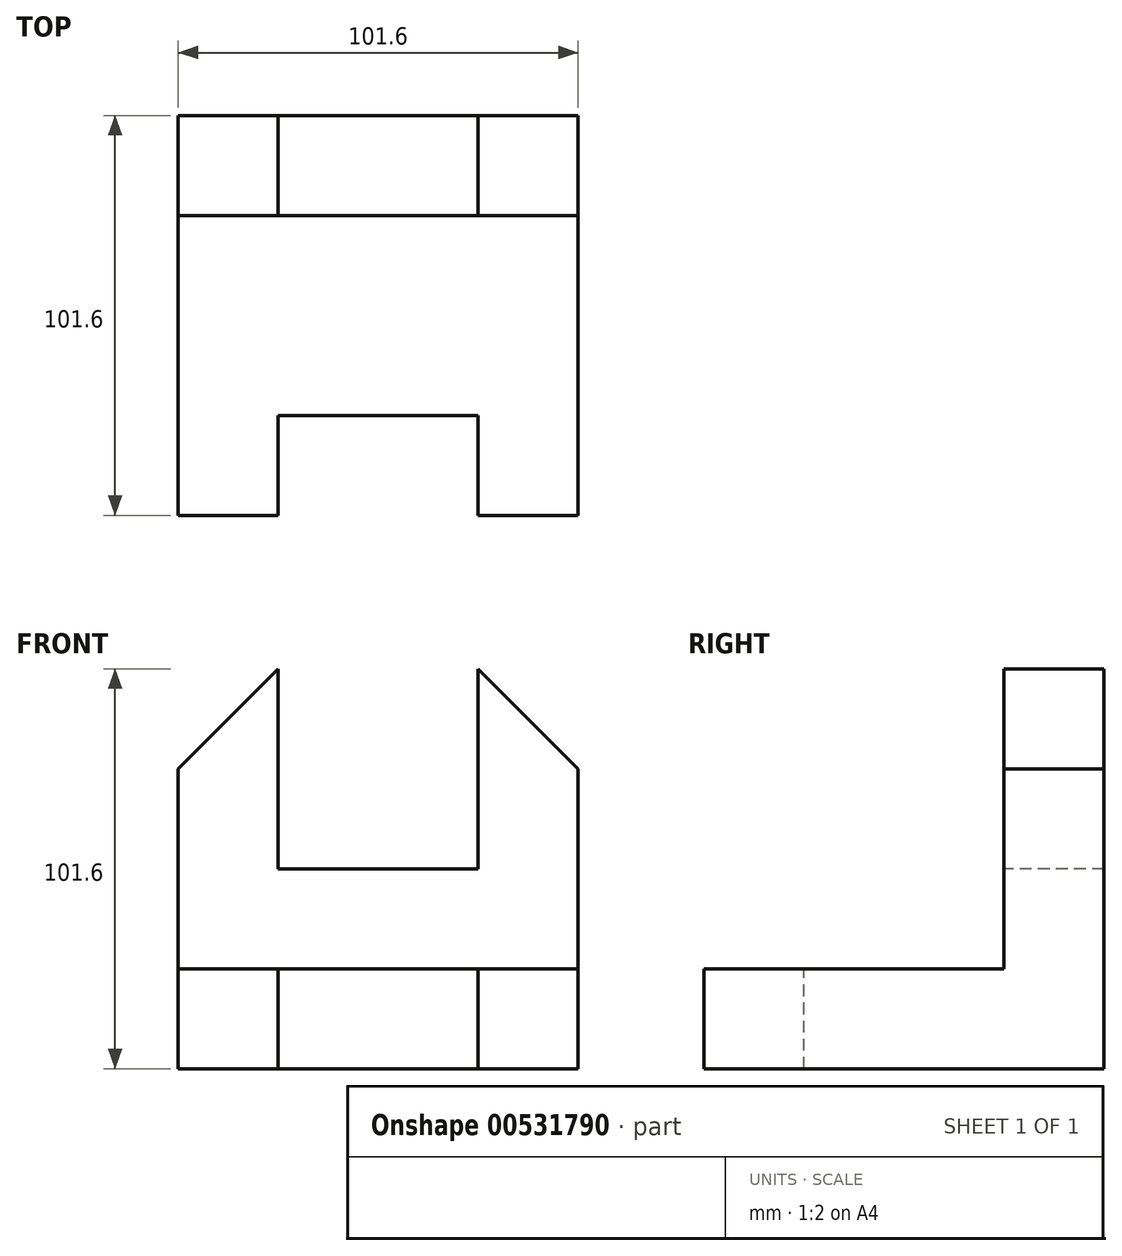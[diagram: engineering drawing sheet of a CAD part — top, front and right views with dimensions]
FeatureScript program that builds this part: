
annotation { "Feature Type Name" : "Feature", "Feature Type Description" : "" }
export const myFeature = defineFeature(function(context is Context, id is Id, definition is map)
    precondition{}
    {
        {
            var Q0;
            Q0=qCreatedBy(makeId("Front.planeOp"),FACE);
            var sketch = newSketch(context, id + "F0", { "sketchPlane" : qUnion([Q0])});
            skLineSegment(sketch, "E0.bottom", {"start": v(-153.66, -86.24) * mm, "end": v(-52.06, -86.24) * mm});
            skLineSegment(sketch, "E0.top", {"start": v(-153.66, 15.36) * mm, "end": v(-52.06, 15.36) * mm});
            skLineSegment(sketch, "E0.left", {"start": v(-153.66, -86.24) * mm, "end": v(-153.66, 15.36) * mm});
            skLineSegment(sketch, "E0.right", {"start": v(-52.06, -86.24) * mm, "end": v(-52.06, 15.36) * mm});
            skSolve(sketch);
        }
        {
            var Q0;
            Q0=makeQuery(id+"F0.imprint","IMPRINT",FACE,{"disambiguationData":[TD([[makeQuery(id+"F0.imprint","IMPRINT",EDGE,{"derivedFrom":sQuery(id+"F0.wireOp",EDGE,"E0.bottom")}),1.0]])]});
            extrude(context, id + "F1", {"entities" : qUnion([Q0]), "depth" : 101.6 * mm, "offsetDistance" : 25.4 * mm});
        }
        {
            var Q0;
            Q0=makeQuery(id+"F1.opExtrude","CAP_FACE",FACE,{"disambiguationData":[OSD([sQuery(id+"F0.wireOp",EDGE,"E0.bottom"),sQuery(id+"F0.wireOp",EDGE,"E0.top"),sQuery(id+"F0.wireOp",EDGE,"E0.left"),sQuery(id+"F0.wireOp",EDGE,"E0.right")])],"isStart":false});
            var sketch = newSketch(context, id + "F2", { "sketchPlane" : qUnion([Q0])});
            skLineSegment(sketch, "E1", {"start": v(-153.66, -86.24) * mm, "end": v(-153.66, -60.84) * mm});
            skLineSegment(sketch, "E2", {"start": v(-153.66, -60.84) * mm, "end": v(-52.06, -60.84) * mm});
            skLineSegment(sketch, "E3.top", {"start": v(-153.66, -10.04) * mm, "end": v(-52.06, -10.04) * mm});
            skLineSegment(sketch, "E3.left", {"start": v(-153.66, -60.84) * mm, "end": v(-153.66, -10.04) * mm});
            skLineSegment(sketch, "E3.right", {"start": v(-52.06, -60.84) * mm, "end": v(-52.06, -10.04) * mm});
            skSolve(sketch);
        }
        {
            var Q0;
            Q0=makeQuery(id+"F2.imprint","IMPRINT",FACE,{"disambiguationData":[TD([[makeQuery(id+"F2.imprint","IMPRINT",EDGE,{"derivedFrom":sQuery(id+"F2.wireOp",EDGE,"E2")}),1.0]])]});
            extrude(context, id + "F3", {"entities" : qUnion([Q0]), "operationType" : NewBodyOperationType.REMOVE, "oppositeDirection" : true, "depth" : 76.2 * mm, "offsetDistance" : 25.4 * mm});
        }
        {
            var Q0;
            {var subQ0=sQuery(id+"F0.wireOp",EDGE,"E0.top");var subQ1=sQuery(id+"F0.wireOp",EDGE,"E0.left");var subQ2=sQuery(id+"F0.wireOp",EDGE,"E0.right");Q0=makeQuery(id+"F3.boolean.opBoolean","SPLIT",FACE,{"disambiguationData":[TD([makeQuery(id+"F1.opExtrude","SWEPT_FACE",FACE,{"disambiguationData":[OSD([subQ0])]})])],"derivedFrom":makeQuery(id+"F1.opExtrude","CAP_FACE",FACE,{"disambiguationData":[OSD([sQuery(id+"F0.wireOp",EDGE,"E0.bottom"),subQ0,subQ1,subQ2])],"isStart":false})});}
            extrude(context, id + "F4", {"entities" : qUnion([Q0]), "operationType" : NewBodyOperationType.REMOVE, "oppositeDirection" : true, "depth" : 76.2 * mm, "offsetDistance" : 25.4 * mm});
        }
        {
            var Q0;
            Q0=makeQuery(id+"F4.boolean.opBoolean","MERGE",FACE,{"derivedFrom":[makeQuery(id+"F3.boolean.opBoolean","COPY",FACE,{"derivedFrom":makeQuery(id+"F3.opExtrude","CAP_FACE",FACE,{"disambiguationData":[OSD([sQuery(id+"F2.wireOp",EDGE,"E2"),sQuery(id+"F2.wireOp",EDGE,"E3.top"),sQuery(id+"F2.wireOp",EDGE,"E3.left"),sQuery(id+"F2.wireOp",EDGE,"E3.right")])],"isStart":false})}),makeQuery(id+"F4.opExtrude","CAP_FACE",FACE,{"disambiguationData":[OSD([sQuery(id+"F0.wireOp",EDGE,"E0.bottom"),sQuery(id+"F0.wireOp",EDGE,"E0.top"),sQuery(id+"F0.wireOp",EDGE,"E0.left"),sQuery(id+"F0.wireOp",EDGE,"E0.right")])],"isStart":false})]});
            var sketch = newSketch(context, id + "F5", { "sketchPlane" : qUnion([Q0])});
            skLineSegment(sketch, "E4.bottom", {"start": v(-153.66, 15.36) * mm, "end": v(-128.26, 15.36) * mm});
            skLineSegment(sketch, "E4.top", {"start": v(-153.66, -35.44) * mm, "end": v(-128.26, -35.44) * mm});
            skLineSegment(sketch, "E4.left", {"start": v(-153.66, 15.36) * mm, "end": v(-153.66, -35.44) * mm});
            skLineSegment(sketch, "E4.right", {"start": v(-128.26, 15.36) * mm, "end": v(-128.26, -35.44) * mm});
            skLineSegment(sketch, "E5.bottom", {"start": v(-52.06, 15.36) * mm, "end": v(-77.46, 15.36) * mm});
            skLineSegment(sketch, "E5.top", {"start": v(-52.06, -35.44) * mm, "end": v(-77.46, -35.44) * mm});
            skLineSegment(sketch, "E5.left", {"start": v(-52.06, 15.36) * mm, "end": v(-52.06, -35.44) * mm});
            skLineSegment(sketch, "E5.right", {"start": v(-77.46, 15.36) * mm, "end": v(-77.46, -35.44) * mm});
            skLineSegment(sketch, "E6", {"start": v(-128.26, -35.44) * mm, "end": v(-77.46, -35.44) * mm});
            skLineSegment(sketch, "E7", {"start": v(-128.26, 15.36) * mm, "end": v(-77.46, 15.36) * mm});
            skSolve(sketch);
        }
        {
            var Q0;
            Q0=makeQuery(id+"F5.imprint","IMPRINT",FACE,{"disambiguationData":[TD([[makeQuery(id+"F5.imprint","IMPRINT",EDGE,{"derivedFrom":sQuery(id+"F5.wireOp",EDGE,"E4.right")}),1.0]])]});
            extrude(context, id + "F6", {"entities" : qUnion([Q0]), "operationType" : NewBodyOperationType.REMOVE, "oppositeDirection" : true, "depth" : 25.4 * mm, "offsetDistance" : 25.4 * mm});
        }
        {
            var Q0;
            Q0=makeQuery(id+"F4.boolean.opBoolean","MERGE",FACE,{"derivedFrom":[makeQuery(id+"F3.boolean.opBoolean","COPY",FACE,{"derivedFrom":makeQuery(id+"F3.opExtrude","CAP_FACE",FACE,{"disambiguationData":[OSD([sQuery(id+"F2.wireOp",EDGE,"E2"),sQuery(id+"F2.wireOp",EDGE,"E3.top"),sQuery(id+"F2.wireOp",EDGE,"E3.left"),sQuery(id+"F2.wireOp",EDGE,"E3.right")])],"isStart":false})}),makeQuery(id+"F4.opExtrude","CAP_FACE",FACE,{"disambiguationData":[OSD([sQuery(id+"F0.wireOp",EDGE,"E0.bottom"),sQuery(id+"F0.wireOp",EDGE,"E0.top"),sQuery(id+"F0.wireOp",EDGE,"E0.left"),sQuery(id+"F0.wireOp",EDGE,"E0.right")])],"isStart":false})]});
            var sketch = newSketch(context, id + "F7", { "sketchPlane" : qUnion([Q0])});
            skLineSegment(sketch, "E8", {"start": v(-153.66, 15.36) * mm, "end": v(-153.66, -10.04) * mm});
            skLineSegment(sketch, "E9", {"start": v(-153.66, -10.04) * mm, "end": v(-128.26, 15.36) * mm});
            skLineSegment(sketch, "E10", {"start": v(-153.66, 15.36) * mm, "end": v(-128.26, 15.36) * mm});
            skLineSegment(sketch, "E11", {"start": v(-52.06, 15.36) * mm, "end": v(-52.06, -10.04) * mm});
            skLineSegment(sketch, "E12", {"start": v(-77.46, 15.36) * mm, "end": v(-52.06, -10.04) * mm});
            skLineSegment(sketch, "E13", {"start": v(-77.46, 15.36) * mm, "end": v(-52.06, 15.36) * mm});
            skSolve(sketch);
        }
        {
            var Q0;
            Q0=makeQuery(id+"F7.imprint","IMPRINT",FACE,{"disambiguationData":[TD([[makeQuery(id+"F7.imprint","IMPRINT",EDGE,{"derivedFrom":sQuery(id+"F7.wireOp",EDGE,"E8")}),-1.0]])]});
            extrude(context, id + "F8", {"entities" : qUnion([Q0]), "operationType" : NewBodyOperationType.REMOVE, "oppositeDirection" : true, "depth" : 25.4 * mm, "offsetDistance" : 25.4 * mm});
        }
        {
            var Q0;
            Q0=makeQuery(id+"F4.boolean.opBoolean","MERGE",FACE,{"derivedFrom":[makeQuery(id+"F3.boolean.opBoolean","COPY",FACE,{"derivedFrom":makeQuery(id+"F3.opExtrude","CAP_FACE",FACE,{"disambiguationData":[OSD([sQuery(id+"F2.wireOp",EDGE,"E2"),sQuery(id+"F2.wireOp",EDGE,"E3.top"),sQuery(id+"F2.wireOp",EDGE,"E3.left"),sQuery(id+"F2.wireOp",EDGE,"E3.right")])],"isStart":false})}),makeQuery(id+"F4.opExtrude","CAP_FACE",FACE,{"disambiguationData":[OSD([sQuery(id+"F0.wireOp",EDGE,"E0.bottom"),sQuery(id+"F0.wireOp",EDGE,"E0.top"),sQuery(id+"F0.wireOp",EDGE,"E0.left"),sQuery(id+"F0.wireOp",EDGE,"E0.right")])],"isStart":false})]});
            var sketch = newSketch(context, id + "F9", { "sketchPlane" : qUnion([Q0])});
            skLineSegment(sketch, "E14", {"start": v(-52.06, 15.36) * mm, "end": v(-52.06, -10.04) * mm});
            skLineSegment(sketch, "E15", {"start": v(-77.46, 15.36) * mm, "end": v(-52.06, -10.04) * mm});
            skLineSegment(sketch, "E16", {"start": v(-77.46, 15.36) * mm, "end": v(-52.06, 15.36) * mm});
            skSolve(sketch);
        }
        {
            var Q0;
            Q0=makeQuery(id+"F9.imprint","IMPRINT",FACE,{"disambiguationData":[TD([[makeQuery(id+"F9.imprint","IMPRINT",EDGE,{"derivedFrom":sQuery(id+"F9.wireOp",EDGE,"E14")}),1.0]])]});
            extrude(context, id + "F10", {"entities" : qUnion([Q0]), "operationType" : NewBodyOperationType.REMOVE, "oppositeDirection" : true, "depth" : 25.4 * mm, "offsetDistance" : 25.4 * mm});
        }
        {
            var Q0;
            Q0=makeQuery(id+"F3.boolean.opBoolean","COPY",FACE,{"derivedFrom":makeQuery(id+"F3.opExtrude","SWEPT_FACE",FACE,{"disambiguationData":[OSD([sQuery(id+"F2.wireOp",EDGE,"E2")])]})});
            var sketch = newSketch(context, id + "F11", { "sketchPlane" : qUnion([Q0])});
            skLineSegment(sketch, "E17.bottom", {"start": v(-153.66, -101.6) * mm, "end": v(-128.26, -101.6) * mm});
            skLineSegment(sketch, "E17.top", {"start": v(-153.66, -76.2) * mm, "end": v(-128.26, -76.2) * mm});
            skLineSegment(sketch, "E17.left", {"start": v(-153.66, -101.6) * mm, "end": v(-153.66, -76.2) * mm});
            skLineSegment(sketch, "E17.right", {"start": v(-128.26, -101.6) * mm, "end": v(-128.26, -76.2) * mm});
            skLineSegment(sketch, "E18.bottom", {"start": v(-52.06, -101.6) * mm, "end": v(-77.46, -101.6) * mm});
            skLineSegment(sketch, "E18.top", {"start": v(-52.06, -76.2) * mm, "end": v(-77.46, -76.2) * mm});
            skLineSegment(sketch, "E18.left", {"start": v(-52.06, -101.6) * mm, "end": v(-52.06, -76.2) * mm});
            skLineSegment(sketch, "E18.right", {"start": v(-77.46, -101.6) * mm, "end": v(-77.46, -76.2) * mm});
            skLineSegment(sketch, "E19", {"start": v(-128.26, -76.2) * mm, "end": v(-77.46, -76.2) * mm});
            skLineSegment(sketch, "E20", {"start": v(-128.26, -101.6) * mm, "end": v(-77.46, -101.6) * mm});
            skSolve(sketch);
        }
        {
            var Q0;
            Q0=makeQuery(id+"F11.imprint","IMPRINT",FACE,{"disambiguationData":[TD([[makeQuery(id+"F11.imprint","IMPRINT",EDGE,{"derivedFrom":sQuery(id+"F11.wireOp",EDGE,"E17.right")}),-1.0]])]});
            extrude(context, id + "F12", {"entities" : qUnion([Q0]), "operationType" : NewBodyOperationType.REMOVE, "oppositeDirection" : true, "depth" : 25.4 * mm, "offsetDistance" : 25.4 * mm});
        }
    });
